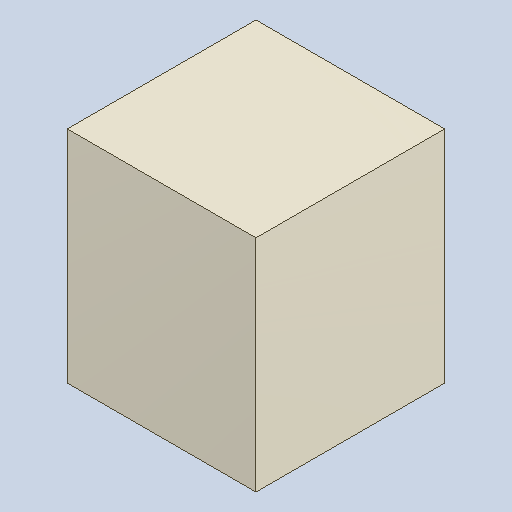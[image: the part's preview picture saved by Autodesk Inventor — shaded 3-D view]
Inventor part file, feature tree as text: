
AUTODESK INVENTOR PART (.ipt)
format: ipt  version: 2023.4 (Build 274418000, 418)  size: 82,944 bytes
history: native  units: mm
features: extrude x1
ambient origin geometry x8: Origin, YZ Plane, XZ Plane, XY Plane, X Axis, Y Axis, Z Axis, Center Point
bodies: Solid1 (feature_tree)
feature tree (1):
  extrude  "Extruded_22"  [1 undecoded]
note: 1 required parameter value undecoded (feature->parameter linkage not recoverable at this tier; creation-order binding heuristic only, values carry confidence <= 0.55)
